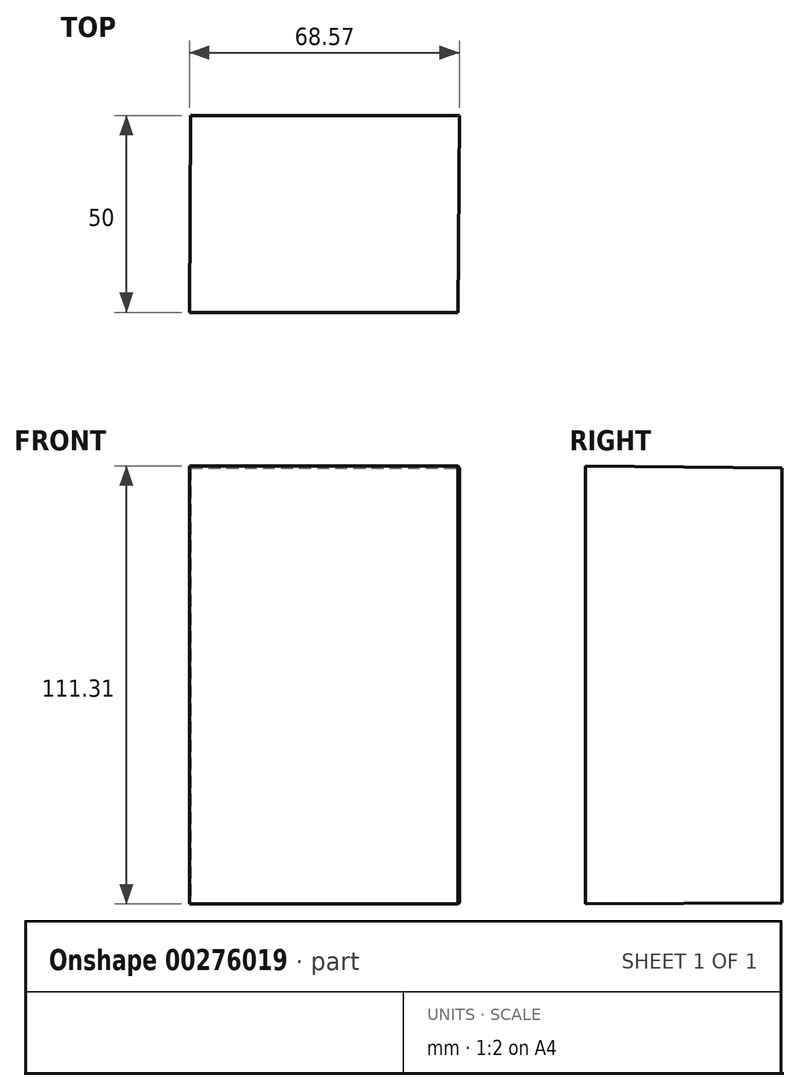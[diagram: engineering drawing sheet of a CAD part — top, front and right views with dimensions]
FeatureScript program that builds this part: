
annotation { "Feature Type Name" : "Feature", "Feature Type Description" : "" }
export const myFeature = defineFeature(function(context is Context, id is Id, definition is map)
    precondition{}
    {
        {
            var Q0;
            Q0=qCreatedBy(makeId("Front.planeOp"),FACE);
            var sketch = newSketch(context, id + "F0", { "sketchPlane" : qUnion([Q0])});
            skLineSegment(sketch, "E0.bottom", {"start": v(-36.72, 55.23) * mm, "end": v(31.56, 55.23) * mm});
            skLineSegment(sketch, "E0.top", {"start": v(-36.72, -55.23) * mm, "end": v(31.56, -55.23) * mm});
            skLineSegment(sketch, "E0.left", {"start": v(-36.72, 55.23) * mm, "end": v(-36.72, -55.23) * mm});
            skLineSegment(sketch, "E0.right", {"start": v(31.56, 55.23) * mm, "end": v(31.56, -55.23) * mm});
            skSolve(sketch);
        }
        {
            var Q0;
            Q0=qCreatedBy(makeId("Front.planeOp"),FACE);
            cPlane(context, id + "F1", {"entities" : qUnion([Q0]), "cplaneType" : CPlaneType.OFFSET, "offset" : 50 * mm, "width" : 150 * mm, "height" : 150 * mm});
        }
        {
            var Q0;
            Q0=qCreatedBy(id+"F1.planeOp",FACE);
            var sketch = newSketch(context, id + "F2", { "sketchPlane" : qUnion([Q0])});
            skLineSegment(sketch, "E1.bottom", {"start": v(-37, 55.8) * mm, "end": v(31.27, 55.8) * mm});
            skLineSegment(sketch, "E1.top", {"start": v(-37, -55.51) * mm, "end": v(31.27, -55.51) * mm});
            skLineSegment(sketch, "E1.left", {"start": v(-37, 55.8) * mm, "end": v(-37, -55.51) * mm});
            skLineSegment(sketch, "E1.right", {"start": v(31.27, 55.8) * mm, "end": v(31.27, -55.51) * mm});
            skSolve(sketch);
        }
        {
            var Q0;
            Q0=makeQuery(id+"F0.imprint","IMPRINT",FACE,{"disambiguationData":[TD([[makeQuery(id+"F0.imprint","IMPRINT",EDGE,{"derivedFrom":sQuery(id+"F0.wireOp",EDGE,"E0.bottom")}),-1.0]])]});
            var Q1;
            Q1=makeQuery(id+"F2.imprint","IMPRINT",FACE,{"disambiguationData":[TD([[makeQuery(id+"F2.imprint","IMPRINT",EDGE,{"derivedFrom":sQuery(id+"F2.wireOp",EDGE,"E1.bottom")}),-1.0]])]});
            loft(context, id + "F3", {"sheetProfilesArray" : [{ "sheetProfileEntities" : qUnion([Q0]) }, { "sheetProfileEntities" : qUnion([Q1]) }]});
        }
    });
